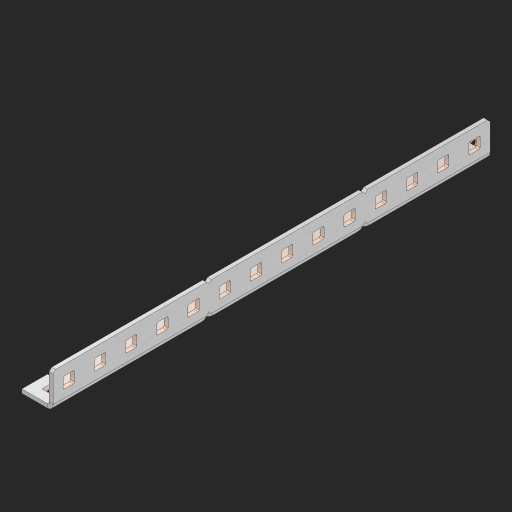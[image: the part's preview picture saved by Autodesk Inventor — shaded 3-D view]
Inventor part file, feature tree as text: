
AUTODESK INVENTOR PART (.ipt)
format: ipt  version: 2023 (Build 270158000, 158)  size: 820,224 bytes
history: native  units: in
note: dims shown in document units (in); Inventor stores cm internally (conversion verified against a paired STEP export)
features: other x190, extrude x40, sheet_metal_op x11, sketch x10, pattern_linear x2, mirror x1, chamfer x1
ambient origin geometry x8: Origin, YZ Plane, XZ Plane, XY Plane, X Axis, Y Axis, Z Axis, Center Point
bodies: Solid1 (feature_tree), Body (feature_tree)
feature tree (255):
  other  "Alu Half C 1x2x1x14"
  other  "Table"
  other  "Alu C 1x2x1x35"
  other  "Alu C 1x2x1x34"
  other  "Alu C 1x2x1x33"
  other  "Alu C 1x2x1x32"
  other  "Alu C 1x2x1x31"
  other  "Alu C 1x2x1x30"
  other  "Alu C 1x2x1x29"
  other  "Alu C 1x2x1x28"
  other  "Alu C 1x2x1x27"
  other  "Alu C 1x2x1x26"
  other  "Alu C 1x2x1x25"
  other  "Alu C 1x2x1x24"
  other  "Alu C 1x2x1x23"
  other  "Alu C 1x2x1x22"
  other  "Alu C 1x2x1x21"
  other  "Alu C 1x2x1x20"
  other  "Alu C 1x2x1x19"
  other  "Alu C 1x2x1x18"
  other  "Alu C 1x2x1x17"
  other  "Alu C 1x2x1x16"
  other  "Alu C 1x2x1x15"
  other  "Alu C 1x2x1x14"
  other  "Alu C 1x2x1x13"
  other  "Alu C 1x2x1x12"
  other  "Alu C 1x2x1x11"
  other  "Alu C 1x2x1x10"
  other  "Alu C 1x2x1x9"
  other  "Alu C 1x2x1x8"
  other  "Alu C 1x2x1x7"
  other  "Alu C 1x2x1x6"
  other  "Alu C 1x2x1x5"
  other  "Alu C 1x2x1x4"
  other  "Alu C 1x2x1x3"
  other  "Alu C 1x2x1x2"
  other  "Alu C 1x2x1x1"
  other  "Steel C 1x2x1x35"
  other  "Steel C 1x2x1x34"
  other  "Steel C 1x2x1x33"
  other  "Steel C 1x2x1x32"
  other  "Steel C 1x2x1x31"
  other  "Steel C 1x2x1x30"
  other  "Steel C 1x2x1x29"
  other  "Steel C 1x2x1x28"
  other  "Steel C 1x2x1x27"
  other  "Steel C 1x2x1x26"
  other  "Steel C 1x2x1x25"
  other  "Steel C 1x2x1x24"
  other  "Steel C 1x2x1x23"
  other  "Steel C 1x2x1x22"
  other  "Steel C 1x2x1x21"
  other  "Steel C 1x2x1x20"
  other  "Steel C 1x2x1x19"
  other  "Steel C 1x2x1x18"
  other  "Steel C 1x2x1x17"
  other  "Steel C 1x2x1x16"
  other  "Steel C 1x2x1x15"
  other  "Steel C 1x2x1x14"
  other  "Steel C 1x2x1x13"
  other  "Steel C 1x2x1x12"
  other  "Steel C 1x2x1x11"
  other  "Steel C 1x2x1x10"
  other  "Steel C 1x2x1x9"
  other  "Steel C 1x2x1x8"
  other  "Steel C 1x2x1x7"
  other  "Steel C 1x2x1x6"
  other  "Steel C 1x2x1x5"
  other  "Steel C 1x2x1x4"
  other  "Steel C 1x2x1x3"
  other  "Steel C 1x2x1x2"
  other  "Steel C 1x2x1x1"
  other  "Alu Half C 1x2x1x35"
  other  "Alu Half C 1x2x1x34"
  other  "Alu Half C 1x2x1x33"
  other  "Alu Half C 1x2x1x32"
  other  "Alu Half C 1x2x1x31"
  other  "Alu Half C 1x2x1x30"
  other  "Alu Half C 1x2x1x29"
  other  "Alu Half C 1x2x1x28"
  other  "Alu Half C 1x2x1x27"
  other  "Alu Half C 1x2x1x26"
  other  "Alu Half C 1x2x1x25"
  other  "Alu Half C 1x2x1x24"
  other  "Alu Half C 1x2x1x23"
  other  "Alu Half C 1x2x1x22"
  other  "Alu Half C 1x2x1x21"
  other  "Alu Half C 1x2x1x20"
  other  "Alu Half C 1x2x1x19"
  other  "Alu Half C 1x2x1x18"
  other  "Alu Half C 1x2x1x17"
  other  "Alu Half C 1x2x1x16"
  other  "Alu Half C 1x2x1x15"
  other  "Alu Half C 1x2x1x13"
  other  "Alu Half C 1x2x1x12"
  other  "Alu Half C 1x2x1x11"
  other  "Alu Half C 1x2x1x10"
  other  "Alu Half C 1x2x1x9"
  other  "Alu Half C 1x2x1x8"
  other  "Alu Half C 1x2x1x7"
  other  "Alu Half C 1x2x1x6"
  other  "Alu Half C 1x2x1x5"
  other  "Alu Half C 1x2x1x4"
  other  "Alu Half C 1x2x1x3"
  other  "Alu Half C 1x2x1x2"
  other  "Alu Half C 1x2x1x1"
  other  "Steel Half C 1x2x1x35"
  other  "Steel Half C 1x2x1x34"
  other  "Steel Half C 1x2x1x33"
  other  "Steel Half C 1x2x1x32"
  other  "Steel Half C 1x2x1x31"
  other  "Steel Half C 1x2x1x30"
  other  "Steel Half C 1x2x1x29"
  other  "Steel Half C 1x2x1x28"
  other  "Steel Half C 1x2x1x27"
  other  "Steel Half C 1x2x1x26"
  other  "Steel Half C 1x2x1x25"
  other  "Steel Half C 1x2x1x24"
  other  "Steel Half C 1x2x1x23"
  other  "Steel Half C 1x2x1x22"
  other  "Steel Half C 1x2x1x21"
  other  "Steel Half C 1x2x1x20"
  other  "Steel Half C 1x2x1x19"
  other  "Steel Half C 1x2x1x18"
  other  "Steel Half C 1x2x1x17"
  other  "Steel Half C 1x2x1x16"
  other  "Steel Half C 1x2x1x15"
  other  "Steel Half C 1x2x1x14"
  other  "Steel Half C 1x2x1x13"
  other  "Steel Half C 1x2x1x12"
  other  "Steel Half C 1x2x1x11"
  other  "Steel Half C 1x2x1x10"
  other  "Steel Half C 1x2x1x9"
  other  "Steel Half C 1x2x1x8"
  other  "Steel Half C 1x2x1x7"
  other  "Steel Half C 1x2x1x6"
  other  "Steel Half C 1x2x1x5"
  other  "Steel Half C 1x2x1x4"
  other  "Steel Half C 1x2x1x3"
  other  "Steel Half C 1x2x1x2"
  other  "Steel Half C 1x2x1x1"
  sheet_metal_op  "Flanges"
  other  "Flange Pattern Plane"
  other  "Flange Pattern Sketch"
  sheet_metal_op  "Flange Pattern"
  sheet_metal_op  "Body Pattern"
  pattern_linear  "Center Pattern"  Spacing1=0.0625in  [1 undecoded]
  other  "Arc Length"
  mirror  "Notch Mirror"
  pattern_linear  "Notch Pattern"  Spacing1=0.182in  [1 undecoded]
  chamfer  "End Chamfer"
  extrude  "Half Cut"  Depth=0.02in
  sketch  "Sketch1"  dims[d0=1.0in]
  other  "Plate1"
  sketch  "Sketch2"  dims[d1=7.0in]
  other  "Plate2"
  sheet_metal_op  "Bend1"
  sheet_metal_op  "Corner1"
  sketch  "Sketch3"  dims[d2=0.0625in]
  sketch  "Sketch7"  dims[d3=0.0625in]
  other  "Srf1"
  other  "Srf2"
  sketch  "Sketch8"  dims[d4=0.0312in]
  sketch  "Sketch9"  dims[d5=0.125in]
  other  "Srf91"
  sheet_metal_op  "Body Pattern Sketch"
  other  "Srf92"
  sketch  "Sketch13"  dims[d6=0.0625in]
  sketch  "Sketch14"  dims[d7=0.5in d8=90.0deg d9=0.0312in]
  sketch  "Sketch15"  dims[d10=0.25in]
  sketch  "Sketch16"  dims[d11=0.0625in d12=0.0625in d16=0.182in d17=0.02in d18=0.0625in d19=0.0in d20=0.25in d21=0.25in d38=5.5118in d40=0.5in d41=0.3937in d43=1.0in d46=0.172in d47=1.0in d48=0.0in d49=0.182in d50=0.02in d51=0.25in d52=0.25in d53=0.0625in d54=0.0in d55=0.172in d56=1.0in d57=0.0in d58=0.25in d60=5.5118in d62=0.5in d63=0.3937in d65=0.5in d85=0.1473in d86=0.1782in d88=0.04in d89=0.0625in d90=0.0in d91=0.04in d92=0.0491in d95=2.5in d96=0.04in d97=0.25in d98=45.0deg d99=0.25in d100=0.5in d101=0.0in d102=2.497in d106=0.182in d107=0.02in d108=0.5in d109=0.5in d110=0.0625in d111=0.0in d112=0.172in d113=0.5in d114=0.0in d117=0.5in d118=0.5in d119=0.5in]
  other  "Srf786"
  other  "Srf823"
  other  "Srf824"
  other  "Srf825"
  other  "Srf826"
  other  "Srf827"
  other  "Srf828"
  other  "Srf829"
  other  "Srf856"
  other  "Srf857"
  other  "Srf858"
  other  "Srf859"
  other  "Srf860"
  other  "Srf861"
  other  "Srf862"
  other  "Srf889"
  other  "Srf890"
  other  "Srf891"
  other  "Srf892"
  other  "Srf893"
  other  "Srf894"
  other  "Srf895"
  other  "Srf896"
  other  "Srf922"
  other  "Srf923"
  other  "Srf924"
  other  "Srf925"
  other  "Srf926"
  other  "Srf959"
  other  "Srf960"
  other  "Srf961"
  other  "Srf962"
  other  "Srf963"
  other  "Srf996"
  other  "Srf997"
  other  "Srf998"
  other  "Srf999"
  other  "Srf1000"
  sheet_metal_op  "Flange Stamp"
  sheet_metal_op  "Flange Circle"
  sheet_metal_op  "Body Stamp"
  sheet_metal_op  "Body Circle"
  other  "Center Stamp"
  other  "Center Circle"
  sheet_metal_op  "Notch"
  extrude  "ExtrusionSrf2"  Depth=0.0625in
  extrude  "ExtrusionSrf92"  TaperAngle=0.0deg  [1 undecoded]
  extrude  "ExtrusionSrf823"  Depth=0.25in
  extrude  "ExtrusionSrf824"  Depth=0.25in
  extrude  "ExtrusionSrf825"  Depth=0.5in
  extrude  "ExtrusionSrf826"  Depth=0.5in
  extrude  "ExtrusionSrf827"  Depth=1.0in TaperAngle=0.0deg
  extrude  "ExtrusionSrf828"  Depth=0.182in
  extrude  "ExtrusionSrf829"  Depth=0.02in
  extrude  "ExtrusionSrf856"  Depth=0.25in
  extrude  "ExtrusionSrf857"  Depth=0.25in
  extrude  "ExtrusionSrf858"  Depth=0.0625in
  extrude  "ExtrusionSrf859"  TaperAngle=0.0deg  [1 undecoded]
  extrude  "ExtrusionSrf860"  Depth=0.5in
  extrude  "ExtrusionSrf861"  Depth=1.0in TaperAngle=0.0deg
  extrude  "ExtrusionSrf862"  Depth=0.25in
  extrude  "ExtrusionSrf889"  Depth=0.5in
  extrude  "ExtrusionSrf890"  Depth=0.5in
  extrude  "ExtrusionSrf891"  Depth=0.5in
  extrude  "ExtrusionSrf892"  Depth=0.5in
  extrude  "ExtrusionSrf893"  Depth=0.5in
  extrude  "ExtrusionSrf894"  Depth=0.0625in
  extrude  "ExtrusionSrf895"  TaperAngle=0.0deg  [1 undecoded]
  extrude  "ExtrusionSrf896"  Depth=0.5in
  extrude  "ExtrusionSrf922"  Depth=0.5in
  extrude  "ExtrusionSrf923"  Depth=2.5in
  extrude  "ExtrusionSrf924"  Depth=0.25in TaperAngle=45.0deg
  extrude  "ExtrusionSrf925"  Depth=0.25in
  extrude  "ExtrusionSrf926"  Depth=0.5in TaperAngle=0.0deg
  extrude  "ExtrusionSrf959"  Depth=0.5in
  extrude  "ExtrusionSrf960"  Depth=0.182in
  extrude  "ExtrusionSrf961"  Depth=0.02in
  extrude  "ExtrusionSrf962"  Depth=0.5in
  extrude  "ExtrusionSrf963"  Depth=0.5in
  extrude  "ExtrusionSrf996"  Depth=0.0625in
  extrude  "ExtrusionSrf997"  TaperAngle=0.0deg  [1 undecoded]
  extrude  "ExtrusionSrf998"  Depth=0.5in
  extrude  "ExtrusionSrf999"  Depth=0.5in TaperAngle=0.0deg
  extrude  "ExtrusionSrf1000"  Depth=0.5in
note: 6 required parameter values undecoded (feature->parameter linkage not recoverable at this tier; creation-order binding heuristic only, values carry confidence <= 0.55)
